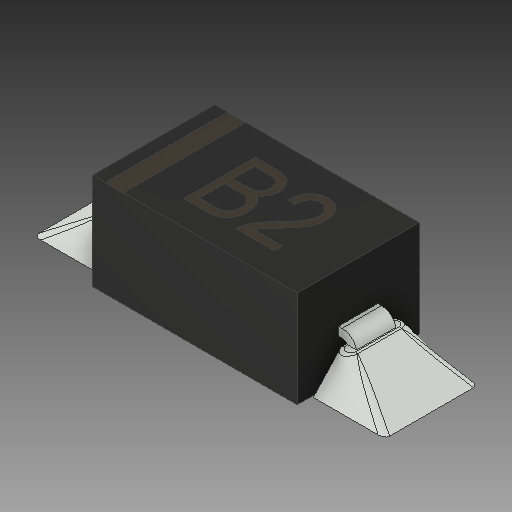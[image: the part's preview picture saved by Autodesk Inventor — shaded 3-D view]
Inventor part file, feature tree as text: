
AUTODESK INVENTOR PART (.ipt)
format: ipt  version: 2019 (Build 230136000, 136)  size: 337,920 bytes
history: native  units: in
note: dims shown in document units (in); Inventor stores cm internally (conversion verified against a paired STEP export)
features: fillet x1
ambient origin geometry x8: Origin, YZ Plane, XZ Plane, XY Plane, X Axis, Y Axis, Z Axis, Center Point
bodies: Solid1 (feature_tree)
feature tree (1):
  fillet  "Fillet9"  [1 undecoded]
note: 1 required parameter value undecoded (feature->parameter linkage not recoverable at this tier; creation-order binding heuristic only, values carry confidence <= 0.55)
